# Revit family: Faucet-Single-Grohe-Allure-23857_Series
name_source: partatom
category: Plumbing Fixtures
units: mm (PartAtom-declared; Revit-internal decimal feet)

## family parameters
Always vertical = No
Cut with Voids When Loaded = No
OmniClass Number = 23.45.55.17
OmniClass Title = Mixing Faucets
Part Type = Normal
Room Calculation Point = No
Round Connector Dimension = Use Diameter
Shared = Yes
Work Plane-Based = Yes

## types (4) — shared parameters
ADA Compliant = Yes
ASME A112.18.1/CSA B125.1 = Yes
Assembly Code = D2020300
CEC Compliant = Yes
CW Connection = No
CWFU = 3
CalGreen Compliant = Yes
Default Elevation = 0"
Description = Allure Single-Hole Single-Handle M-Size Bathroom Faucet 1.2 GPM
Flow Rate = 1.2 gpm
GROHE DreamSpray = Yes
GROHE EcoJoy = Yes
GROHE StarLight = Yes
HW Connection = No
HWFU = 3
Height = 7 7/8"
IAPMO Compliance = • WaterSense • Low Lead Certified • Massachusetts Plumbing Board Approved • Energy Policy Act of 1992 • NSF 61• NSF 372 • Complies with lead plumbing laws
Installation Type = Surface Mounted
Length = 4 5/8"
Manufacturer = GROHE
Plate Width = 2 3/16"
Price = Prices may vary. Please consult Manufacturer Representative for most up-to-date price list.
Product Documentation Link = https://lixil.cdn.celum.cloud
Product Page URL = https://www.grohe.us
Spout Height = 7"
Tempered Water Connection = Yes
Tempered Water Connection Diameter = 1/2"
Vent Connection = No
WFU = 4
Waste Connection = No
Width = 4"

## per-type parameters (varying)
| type | Finish | Material | URL |
| 23857001 | Metal-Grohe-001-StarLight Chrome | Metal-Grohe-001-StarLight Chrome | https://www.grohe.com |
| 23857EN1 | Metal-Grohe-EN1-Brushed Nickel InfinityFinish | Metal-Grohe-EN1-Brushed Nickel InfinityFinish | https://www.grohe.us |
| 23857GN1 | Metal-Grohe-GN1-Brushed Cool Sunrise | Metal-Grohe-GN1-Brushed Cool Sunrise | https://www.grohe.us |
| 238572431 | Metal-Grohe-2431-Matte Black | Metal-Grohe-2431-Matte Black | https://www.grohe.us |

note: column(s) folded — value = type name in every type: Model

## geometry (parser evidence)
native form markers: Sweep x2
no freeform markers — native parametric forms only
